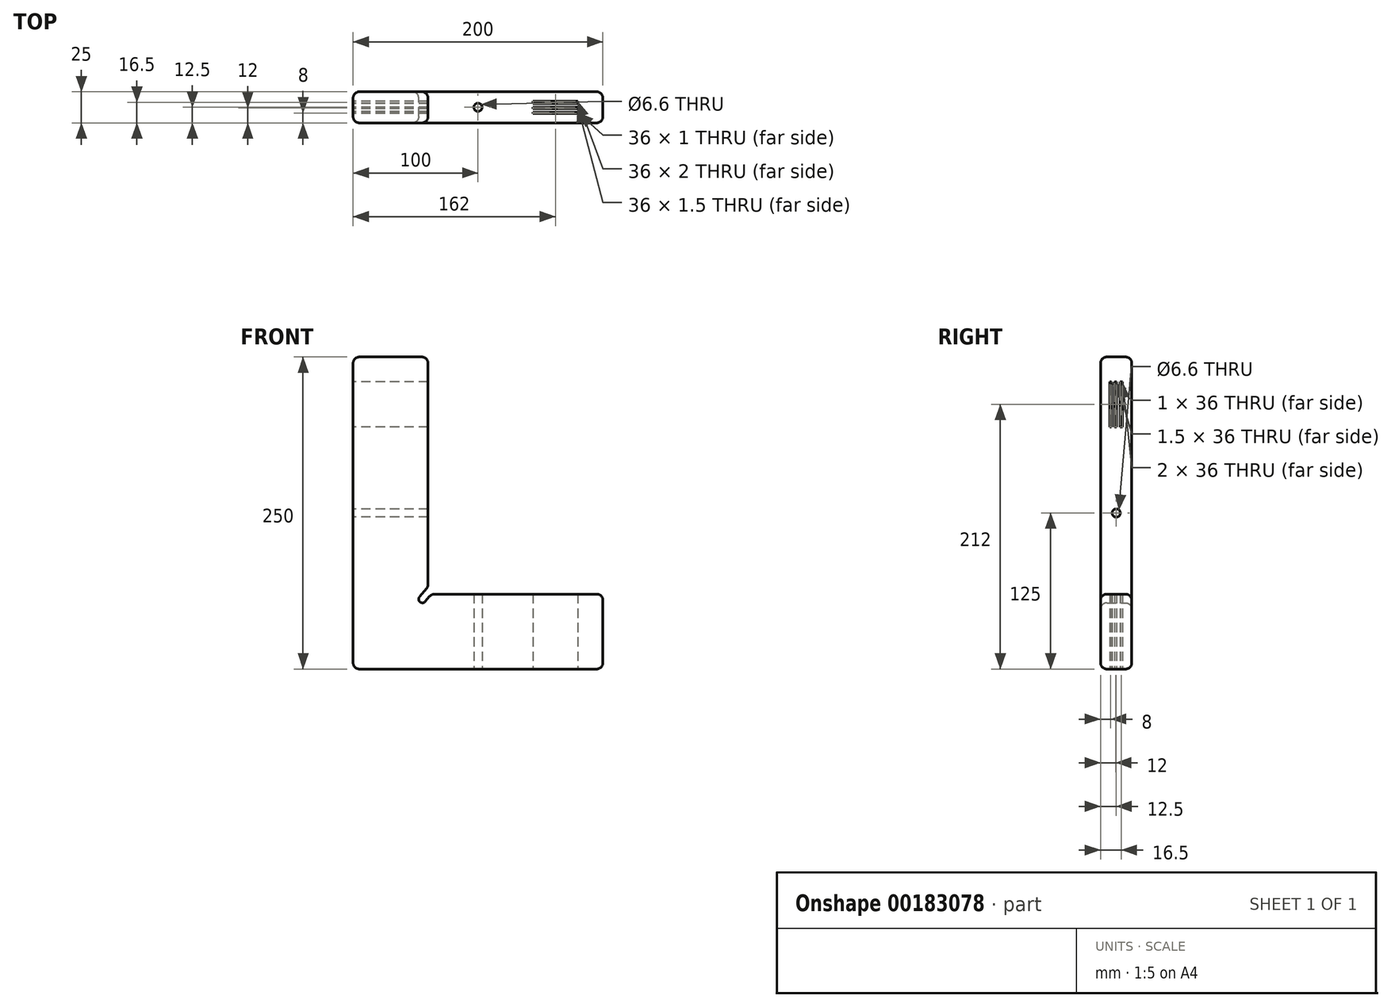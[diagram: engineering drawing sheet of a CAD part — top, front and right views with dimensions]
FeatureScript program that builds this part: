
annotation { "Feature Type Name" : "Feature", "Feature Type Description" : "" }
export const myFeature = defineFeature(function(context is Context, id is Id, definition is map)
    precondition{}
    {
        {
            var Q0;
            Q0=qCreatedBy(makeId("Front.planeOp"),FACE);
            var sketch = newSketch(context, id + "F0", { "sketchPlane" : qUnion([Q0])});
            skLineSegment(sketch, "E0", {"start": v(0, 0) * mm, "end": v(-200, 0) * mm});
            skLineSegment(sketch, "E1", {"start": v(-200, 0) * mm, "end": v(-200, 250) * mm});
            skLineSegment(sketch, "E2", {"start": v(-200, 250) * mm, "end": v(-140, 250) * mm});
            skLineSegment(sketch, "E3", {"start": v(-140, 250) * mm, "end": v(-140, 66.03) * mm});
            skLineSegment(sketch, "E4", {"start": v(-137.23, 60) * mm, "end": v(0, 60) * mm});
            skLineSegment(sketch, "E5", {"start": v(0, 60) * mm, "end": v(0, 0) * mm});
            skArc(sketch, "E6", {"start": v(-146.8, 57.93) * mm, "mid": v(-146.43, 53.7) * mm, "end": v(-142.2, 54.07) * mm});
            skLineSegment(sketch, "E7", {"start": v(-146.8, 57.93) * mm, "end": v(-140, 66.03) * mm});
            skLineSegment(sketch, "E8", {"start": v(-142.2, 54.07) * mm, "end": v(-137.23, 60) * mm});
            skSolve(sketch);
        }
        {
            var Q0;
            Q0=makeQuery(id+"F0.imprint","IMPRINT",FACE,{"disambiguationData":[TD([[makeQuery(id+"F0.imprint","IMPRINT",EDGE,{"derivedFrom":sQuery(id+"F0.wireOp",EDGE,"E0")}),-1.0]])]});
            extrude(context, id + "F1", {"entities" : qUnion([Q0]), "depth" : 25 * mm});
        }
        {
            var Q0;
            Q0=makeQuery(id+"F1.opExtrude","CAP_EDGE",EDGE,{"disambiguationData":[OSD([sQuery(id+"F0.wireOp",EDGE,"E1")])],"isStart":false});
            var Q1;
            Q1=makeQuery(id+"F1.opExtrude","CAP_FACE",FACE,{"disambiguationData":[OSD([sQuery(id+"F0.wireOp",EDGE,"E0"),sQuery(id+"F0.wireOp",EDGE,"E1"),sQuery(id+"F0.wireOp",EDGE,"E2"),sQuery(id+"F0.wireOp",EDGE,"E3"),sQuery(id+"F0.wireOp",EDGE,"E4"),sQuery(id+"F0.wireOp",EDGE,"E5"),sQuery(id+"F0.wireOp",EDGE,"E6"),sQuery(id+"F0.wireOp",EDGE,"E7"),sQuery(id+"F0.wireOp",EDGE,"E8")])],"isStart":false});
            var Q2;
            Q2=makeQuery(id+"F1.opExtrude","CAP_EDGE",EDGE,{"disambiguationData":[OSD([sQuery(id+"F0.wireOp",EDGE,"E0")])],"isStart":true});
            var Q3;
            Q3=makeQuery(id+"F1.opExtrude","SWEPT_EDGE",EDGE,{"disambiguationData":[OSD([sQuery(id+"F0.wireOp",EDGE,"E0"),sQuery(id+"F0.wireOp",EDGE,"E1")])]});
            var Q4;
            Q4=makeQuery(id+"F1.opExtrude","CAP_EDGE",EDGE,{"disambiguationData":[OSD([sQuery(id+"F0.wireOp",EDGE,"E1")])],"isStart":true});
            var Q5;
            Q5=makeQuery(id+"F1.opExtrude","CAP_FACE",FACE,{"disambiguationData":[OSD([sQuery(id+"F0.wireOp",EDGE,"E0"),sQuery(id+"F0.wireOp",EDGE,"E1"),sQuery(id+"F0.wireOp",EDGE,"E2"),sQuery(id+"F0.wireOp",EDGE,"E3"),sQuery(id+"F0.wireOp",EDGE,"E4"),sQuery(id+"F0.wireOp",EDGE,"E5"),sQuery(id+"F0.wireOp",EDGE,"E6"),sQuery(id+"F0.wireOp",EDGE,"E7"),sQuery(id+"F0.wireOp",EDGE,"E8")])],"isStart":true});
            var Q6;
            Q6=makeQuery(id+"F1.opExtrude","SWEPT_EDGE",EDGE,{"disambiguationData":[OSD([sQuery(id+"F0.wireOp",EDGE,"E0"),sQuery(id+"F0.wireOp",EDGE,"E5")])]});
            var Q7;
            Q7=makeQuery(id+"F1.opExtrude","SWEPT_EDGE",EDGE,{"disambiguationData":[OSD([sQuery(id+"F0.wireOp",EDGE,"E4"),sQuery(id+"F0.wireOp",EDGE,"E5")])]});
            var Q8;
            Q8=makeQuery(id+"F1.opExtrude","SWEPT_EDGE",EDGE,{"disambiguationData":[OSD([sQuery(id+"F0.wireOp",EDGE,"E4"),sQuery(id+"F0.wireOp",EDGE,"E8")])]});
            var Q9;
            Q9=makeQuery(id+"F1.opExtrude","SWEPT_FACE",FACE,{"disambiguationData":[OSD([sQuery(id+"F0.wireOp",EDGE,"E3")])]});
            fillet(context, id + "F2", {"entities" : qUnion([Q0, Q1, Q2, Q3, Q4, Q5, Q6, Q7, Q8, Q9]), "radius" : 5 * mm, "tangentPropagation" : true, "allowEdgeOverflow" : false});
        }
        {
            var Q0;
            Q0=makeQuery(id+"F1.opExtrude","SWEPT_EDGE",EDGE,{"disambiguationData":[OSD([sQuery(id+"F0.wireOp",EDGE,"E1"),sQuery(id+"F0.wireOp",EDGE,"E2")])]});
            fillet(context, id + "F3", {"entities" : qUnion([Q0]), "radius" : 5 * mm, "tangentPropagation" : true, "allowEdgeOverflow" : false});
        }
        {
            var Q0;
            Q0=makeQuery(id+"F1.opExtrude","SWEPT_FACE",FACE,{"disambiguationData":[OSD([sQuery(id+"F0.wireOp",EDGE,"E0")])]});
            var sketch = newSketch(context, id + "F4", { "sketchPlane" : qUnion([Q0])});
            skLineSegment(sketch, "E9", {"start": v(-20, 7.5) * mm, "end": v(-56, 7.5) * mm});
            skLineSegment(sketch, "E10", {"start": v(-56, 7.5) * mm, "end": v(-56, 9.5) * mm});
            skLineSegment(sketch, "E11", {"start": v(-56, 9.5) * mm, "end": v(-20, 9.5) * mm});
            skLineSegment(sketch, "E12", {"start": v(-20, 9.5) * mm, "end": v(-20, 7.5) * mm});
            skLineSegment(sketch, "E13", {"start": v(-56, 17.5) * mm, "end": v(-56, 16.5) * mm});
            skLineSegment(sketch, "E14", {"start": v(-56, 16.5) * mm, "end": v(-20, 16.5) * mm});
            skLineSegment(sketch, "E15", {"start": v(-20, 16.5) * mm, "end": v(-20, 17.5) * mm});
            skLineSegment(sketch, "E16", {"start": v(-20, 17.5) * mm, "end": v(-56, 17.5) * mm});
            skLineSegment(sketch, "E17", {"start": v(-56, 13.75) * mm, "end": v(-20, 13.75) * mm});
            skLineSegment(sketch, "E18", {"start": v(-20, 13.75) * mm, "end": v(-20, 12.25) * mm});
            skLineSegment(sketch, "E19", {"start": v(-20, 12.25) * mm, "end": v(-56, 12.25) * mm});
            skLineSegment(sketch, "E20", {"start": v(-56, 12.25) * mm, "end": v(-56, 13.75) * mm});
            skSolve(sketch);
        }
        {
            var Q0;
            Q0=makeQuery(id+"F4.imprint","IMPRINT",FACE,{"disambiguationData":[TD([[makeQuery(id+"F4.imprint","IMPRINT",EDGE,{"derivedFrom":sQuery(id+"F4.wireOp",EDGE,"E13")}),1.0]])]});
            var Q1;
            Q1=makeQuery(id+"F4.imprint","IMPRINT",FACE,{"disambiguationData":[TD([[makeQuery(id+"F4.imprint","IMPRINT",EDGE,{"derivedFrom":sQuery(id+"F4.wireOp",EDGE,"E17")}),-1.0]])]});
            var Q2;
            Q2=makeQuery(id+"F4.imprint","IMPRINT",FACE,{"disambiguationData":[TD([[makeQuery(id+"F4.imprint","IMPRINT",EDGE,{"derivedFrom":sQuery(id+"F4.wireOp",EDGE,"E9")}),-1.0]])]});
            extrude(context, id + "F5", {"entities" : qUnion([Q0, Q1, Q2]), "operationType" : NewBodyOperationType.REMOVE, "oppositeDirection" : true, "depth" : 64.1 * mm});
        }
        {
            var Q0;
            Q0=makeQuery(id+"F1.opExtrude","SWEPT_FACE",FACE,{"disambiguationData":[OSD([sQuery(id+"F0.wireOp",EDGE,"E0")])]});
            var sketch = newSketch(context, id + "F6", { "sketchPlane" : qUnion([Q0])});
            skPoint(sketch, "E21", {"position": v(-100, 12.5) * mm});
            skSolve(sketch);
        }
        {
            var Q0;
            Q0=sQuery(id+"F6.wireOp",VERTEX,"E21");
            var Q1;
            Q1=makeQuery(id+"F1.opExtrude","SWEPT_BODY",BODY,{"disambiguationData":[OSD([sQuery(id+"F0.wireOp",EDGE,"E0"),sQuery(id+"F0.wireOp",EDGE,"E1"),sQuery(id+"F0.wireOp",EDGE,"E2"),sQuery(id+"F0.wireOp",EDGE,"E3"),sQuery(id+"F0.wireOp",EDGE,"E4"),sQuery(id+"F0.wireOp",EDGE,"E5"),sQuery(id+"F0.wireOp",EDGE,"E6"),sQuery(id+"F0.wireOp",EDGE,"E7"),sQuery(id+"F0.wireOp",EDGE,"E8")])]});
            hole(context, id + "F7", {"style" : HoleStyle.SIMPLE, "endStyle" : HoleEndStyle.THROUGH, "standardTappedOrClearance" : lookupTablePath({ "standard" : "ISO", "fit" : "Normal", "size" : "M6", "type" : "Clearance" }), "standardBlindInLast" : lookupTablePath({ "fit" : "Standard", "standard" : "ISO", "size" : "M6", "type" : "Clearance" }), "holeDiameter" : 6.6 * mm, "locations" : qUnion([Q0]), "scope" : qUnion([Q1]), "isTappedThrough" : true});
        }
        {
            var Q0;
            Q0=makeQuery(id+"F1.opExtrude","SWEPT_FACE",FACE,{"disambiguationData":[OSD([sQuery(id+"F0.wireOp",EDGE,"E1")])]});
            var sketch = newSketch(context, id + "F8", { "sketchPlane" : qUnion([Q0])});
            skLineSegment(sketch, "E22", {"start": v(7.5, 194) * mm, "end": v(7.5, 230) * mm});
            skLineSegment(sketch, "E23", {"start": v(7.5, 230) * mm, "end": v(9.5, 230) * mm});
            skLineSegment(sketch, "E24", {"start": v(9.5, 230) * mm, "end": v(9.5, 194) * mm});
            skLineSegment(sketch, "E25", {"start": v(9.5, 194) * mm, "end": v(7.5, 194) * mm});
            skLineSegment(sketch, "E26", {"start": v(17.5, 230) * mm, "end": v(16.5, 230) * mm});
            skLineSegment(sketch, "E27", {"start": v(16.5, 230) * mm, "end": v(16.5, 194) * mm});
            skLineSegment(sketch, "E28", {"start": v(16.5, 194) * mm, "end": v(17.5, 194) * mm});
            skLineSegment(sketch, "E29", {"start": v(17.5, 194) * mm, "end": v(17.5, 230) * mm});
            skLineSegment(sketch, "E30", {"start": v(13.75, 230) * mm, "end": v(13.75, 194) * mm});
            skLineSegment(sketch, "E31", {"start": v(13.75, 194) * mm, "end": v(12.25, 194) * mm});
            skLineSegment(sketch, "E32", {"start": v(12.25, 194) * mm, "end": v(12.25, 230) * mm});
            skLineSegment(sketch, "E33", {"start": v(12.25, 230) * mm, "end": v(13.75, 230) * mm});
            skSolve(sketch);
        }
        {
            var Q0;
            Q0 = qSketchRegion(id + "F8", true);
            extrude(context, id + "F9", {"entities" : qUnion([Q0]), "operationType" : NewBodyOperationType.REMOVE, "oppositeDirection" : true, "depth" : 69 * mm});
        }
        {
            var Q0;
            Q0=makeQuery(id+"F1.opExtrude","SWEPT_FACE",FACE,{"disambiguationData":[OSD([sQuery(id+"F0.wireOp",EDGE,"E1")])]});
            var sketch = newSketch(context, id + "F10", { "sketchPlane" : qUnion([Q0])});
            skPoint(sketch, "E34", {"position": v(12.5, 125) * mm});
            skSolve(sketch);
        }
        {
            var Q0;
            Q0=sQuery(id+"F10.wireOp",VERTEX,"E34");
            var Q1;
            Q1=makeQuery(id+"F1.opExtrude","SWEPT_BODY",BODY,{"disambiguationData":[OSD([sQuery(id+"F0.wireOp",EDGE,"E0"),sQuery(id+"F0.wireOp",EDGE,"E1"),sQuery(id+"F0.wireOp",EDGE,"E2"),sQuery(id+"F0.wireOp",EDGE,"E3"),sQuery(id+"F0.wireOp",EDGE,"E4"),sQuery(id+"F0.wireOp",EDGE,"E5"),sQuery(id+"F0.wireOp",EDGE,"E6"),sQuery(id+"F0.wireOp",EDGE,"E7"),sQuery(id+"F0.wireOp",EDGE,"E8")])]});
            hole(context, id + "F11", {"style" : HoleStyle.SIMPLE, "endStyle" : HoleEndStyle.THROUGH, "standardTappedOrClearance" : lookupTablePath({ "standard" : "ISO", "fit" : "Normal", "size" : "M6", "type" : "Clearance" }), "standardBlindInLast" : lookupTablePath({ "fit" : "Standard", "standard" : "ISO", "size" : "M6", "type" : "Clearance" }), "holeDiameter" : 6.6 * mm, "locations" : qUnion([Q0]), "scope" : qUnion([Q1]), "isTappedThrough" : true});
        }
    });
